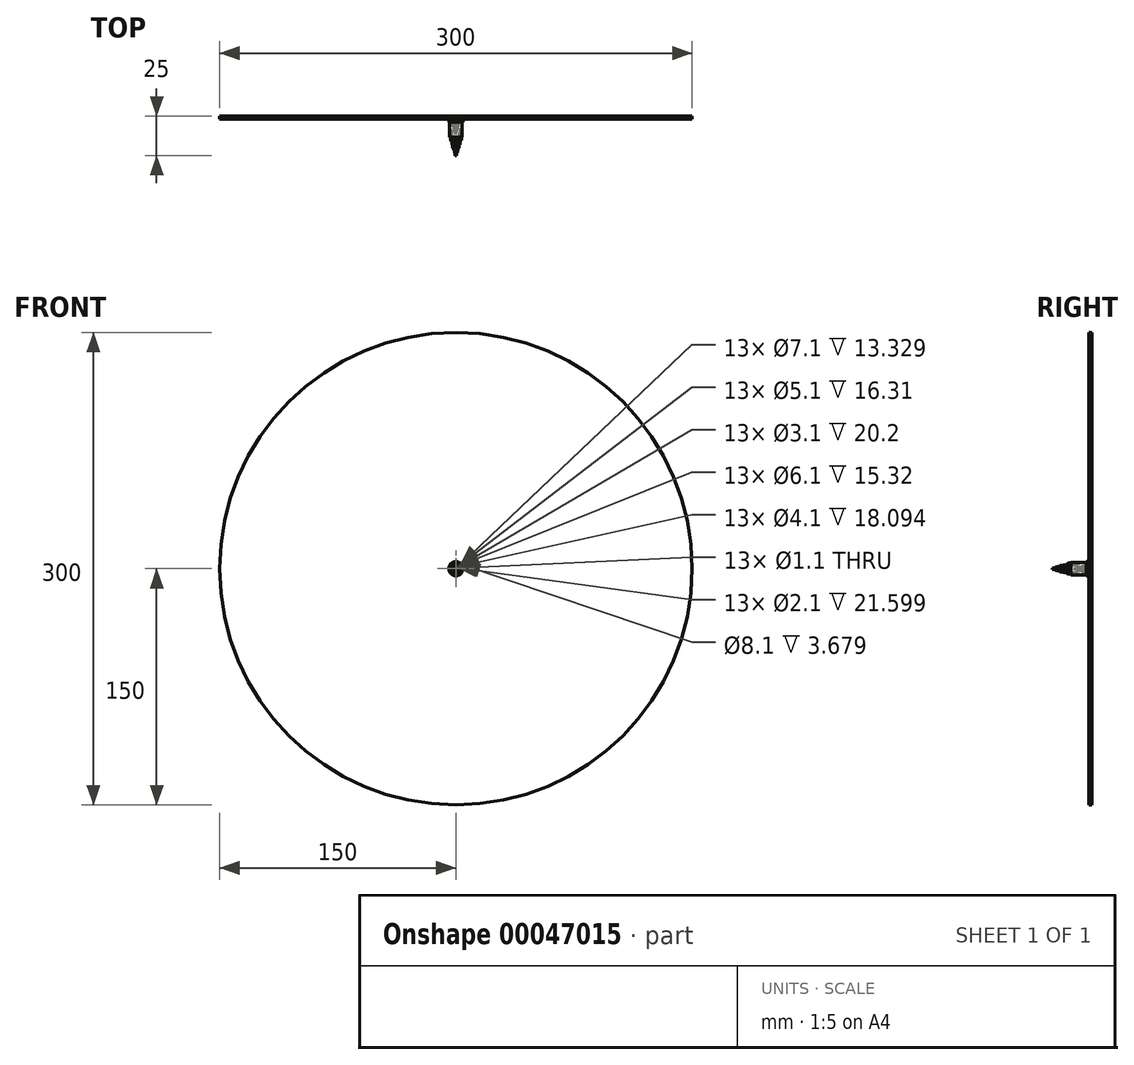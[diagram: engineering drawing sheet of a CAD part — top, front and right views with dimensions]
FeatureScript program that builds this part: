
annotation { "Feature Type Name" : "Feature", "Feature Type Description" : "" }
export const myFeature = defineFeature(function(context is Context, id is Id, definition is map)
    precondition{}
    {
        {
            var Q0;
            Q0=qCreatedBy(makeId("Front.planeOp"),FACE);
            var sketch = newSketch(context, id + "F0", { "sketchPlane" : qUnion([Q0])});
            skCircle(sketch, "E0", {"center": v(0, 0) * mm, "radius": 0.5 * mm});
            skCircle(sketch, "E1", {"center": v(0, 0) * mm, "radius": 1 * mm});
            skCircle(sketch, "E2.0", {"center": v(0, 0) * mm, "radius": 0.55 * mm});
            skCircle(sketch, "E3", {"center": v(0, 0) * mm, "radius": 1.5 * mm});
            skCircle(sketch, "E4.0", {"center": v(0, 0) * mm, "radius": 1.05 * mm});
            skCircle(sketch, "E5", {"center": v(0, 0) * mm, "radius": 2 * mm});
            skCircle(sketch, "E6.0", {"center": v(0, 0) * mm, "radius": 1.55 * mm});
            skCircle(sketch, "E7", {"center": v(0, 0) * mm, "radius": 2.5 * mm});
            skCircle(sketch, "E8.0", {"center": v(0, 0) * mm, "radius": 2.05 * mm});
            skCircle(sketch, "E9", {"center": v(0, 0) * mm, "radius": 3 * mm});
            skCircle(sketch, "E10.0", {"center": v(0, 0) * mm, "radius": 2.55 * mm});
            skCircle(sketch, "E11", {"center": v(0, 0) * mm, "radius": 3.5 * mm});
            skCircle(sketch, "E12.0", {"center": v(0, 0) * mm, "radius": 3.05 * mm});
            skCircle(sketch, "E13", {"center": v(0, 0) * mm, "radius": 4 * mm});
            skCircle(sketch, "E14.0", {"center": v(0, 0) * mm, "radius": 3.55 * mm});
            skCircle(sketch, "E15", {"center": v(0, 0) * mm, "radius": 4.5 * mm});
            skCircle(sketch, "E16.0", {"center": v(0, 0) * mm, "radius": 4.05 * mm});
            skSolve(sketch);
        }
        {
            var Q0;
            Q0=qCreatedBy(makeId("Front.planeOp"),FACE);
            var sketch = newSketch(context, id + "F1", { "sketchPlane" : qUnion([Q0])});
            skCircle(sketch, "E17", {"center": v(0, 0) * mm, "radius": 150 * mm});
            skCircle(sketch, "E18", {"center": v(0, 0) * mm, "radius": 4.5 * mm});
            skSolve(sketch);
        }
        {
            var Q0;
            Q0=makeQuery(id+"F0.imprint","IMPRINT",FACE,{"disambiguationData":[TD([[makeQuery(id+"F0.imprint","IMPRINT",EDGE,{"derivedFrom":sQuery(id+"F0.wireOp",EDGE,"E0")}),1.0]])]});
            extrude(context, id + "F2", {"entities" : qUnion([Q0]), "depth" : 25 * mm});
        }
        {
            var Q0;
            Q0=makeQuery(id+"F0.imprint","IMPRINT",FACE,{"disambiguationData":[TD([[makeQuery(id+"F0.imprint","IMPRINT",EDGE,{"derivedFrom":sQuery(id+"F0.wireOp",EDGE,"E1")}),1.0]])]});
            extrude(context, id + "F3", {"entities" : qUnion([Q0]), "depth" : 23.24 * mm});
        }
        {
            var Q0;
            Q0=makeQuery(id+"F0.imprint","IMPRINT",FACE,{"disambiguationData":[TD([[makeQuery(id+"F0.imprint","IMPRINT",EDGE,{"derivedFrom":sQuery(id+"F0.wireOp",EDGE,"E3")}),1.0]])]});
            extrude(context, id + "F4", {"entities" : qUnion([Q0]), "depth" : 21.6 * mm});
        }
        {
            var Q0;
            Q0=makeQuery(id+"F0.imprint","IMPRINT",FACE,{"disambiguationData":[TD([[makeQuery(id+"F0.imprint","IMPRINT",EDGE,{"derivedFrom":sQuery(id+"F0.wireOp",EDGE,"E5")}),1.0]])]});
            extrude(context, id + "F5", {"entities" : qUnion([Q0]), "depth" : 20.2 * mm});
        }
        {
            var Q0;
            Q0=makeQuery(id+"F0.imprint","IMPRINT",FACE,{"disambiguationData":[TD([[makeQuery(id+"F0.imprint","IMPRINT",EDGE,{"derivedFrom":sQuery(id+"F0.wireOp",EDGE,"E7")}),1.0]])]});
            extrude(context, id + "F6", {"entities" : qUnion([Q0]), "depth" : 18.1 * mm});
        }
        {
            var Q0;
            Q0=makeQuery(id+"F0.imprint","IMPRINT",FACE,{"disambiguationData":[TD([[makeQuery(id+"F0.imprint","IMPRINT",EDGE,{"derivedFrom":sQuery(id+"F0.wireOp",EDGE,"E9")}),1.0]])]});
            extrude(context, id + "F7", {"entities" : qUnion([Q0]), "depth" : 16.3 * mm});
        }
        {
            var Q0;
            Q0=makeQuery(id+"F0.imprint","IMPRINT",FACE,{"disambiguationData":[TD([[makeQuery(id+"F0.imprint","IMPRINT",EDGE,{"derivedFrom":sQuery(id+"F0.wireOp",EDGE,"E11")}),1.0]])]});
            extrude(context, id + "F8", {"entities" : qUnion([Q0]), "depth" : 15.32 * mm});
        }
        {
            var Q0;
            Q0=makeQuery(id+"F0.imprint","IMPRINT",FACE,{"disambiguationData":[TD([[makeQuery(id+"F0.imprint","IMPRINT",EDGE,{"derivedFrom":sQuery(id+"F0.wireOp",EDGE,"E13")}),1.0]])]});
            extrude(context, id + "F9", {"entities" : qUnion([Q0]), "depth" : 13.33 * mm});
        }
        {
            var Q0;
            Q0=makeQuery(id+"F0.imprint","IMPRINT",FACE,{"disambiguationData":[TD([[makeQuery(id+"F0.imprint","IMPRINT",EDGE,{"derivedFrom":sQuery(id+"F0.wireOp",EDGE,"E15")}),1.0]])]});
            extrude(context, id + "F10", {"entities" : qUnion([Q0]), "depth" : 3.68 * mm});
        }
        {
            var Q0;
            Q0=makeQuery(id+"F1.imprint","IMPRINT",FACE,{"disambiguationData":[TD([[makeQuery(id+"F1.imprint","IMPRINT",EDGE,{"derivedFrom":sQuery(id+"F1.wireOp",EDGE,"E17")}),1.0]])]});
            extrude(context, id + "F11", {"entities" : qUnion([Q0]), "operationType" : NewBodyOperationType.ADD, "depth" : 2 * mm});
        }
    });
